# Revit family: Sink-Vessel-Lavatory-KOHLER-Forefront-K-5373IN_1
name_source: partatom
category: Plumbing Fixtures
units: mm (PartAtom-declared; Revit-internal decimal feet)

## family parameters
Cut with Voids When Loaded = No
Host = Face
OmniClass Number = 23.31.13.00
OmniClass Title = Sinks
Part Type = Normal
Room Calculation Point = No
Round Connector Dimension = Use Diameter
Shared = No

## types (5) — shared parameters
ADA Compliant = No
Assembly Code = D2010400
CW Connection = No
Cold Water Inlet = Cold Water Inlet
Date Modified = 12/05/2023
Default Elevation = 36"
Description = Vessel bathroom sink
Drain Included = No
Flow Rate = 0 GPM
HW Connection = No
Height = 6 7/8"
Hot Water Inlet = Hot Water Inlet
Length = 22 5/8"
Manufacturer = Kohler Co.
Master Format 2014 = 22 41 16
Master Format 2014 Name = Residential Lavatories and Sinks
Material = Vitreous China
Pressure = 0.00 psi
Product Documentation Link = http://resources.kohler.com
Product Name = Forefront
URL = https://www.kohler.co.in
Vent Connection = No
Waste Connection = Yes
Waste Water Outlet = Waste Water Outlet
WaterSense Certified = No
Width = 16 1/8"

## per-type parameters (varying)
| type | Finish | Model | Product Page URL | Type |
| 0-White | Kohler-Vitreous_China-0-White | K-5373IN-0 | https://www.kohler.co.in | 1 |
| HG1-Honed Thunder Grey | Kohler-Vitreous_China-HG1-Honed_Thunder_Grey | K-5373IN-HG1 | https://www.kohler.co.in | 2 |
| HP1-Honed Peacock | Kohler-Vitreous_China-HP1-Honed_Peacock | K-5373IN-HP1 |  | 3 |
| HT1-Honed Truffle | Kohler-Vitreous_China-HT1-Honed_Truffle | K-5373IN-HT1 |  | 4 |
| DGS-Indigo | KOHLER-Vitreous_China-DGS-Indigo | K-5373IN-DGS |  | 5 |

## geometry (parser evidence)
native form markers: Sweep x5
no freeform markers — native parametric forms only
